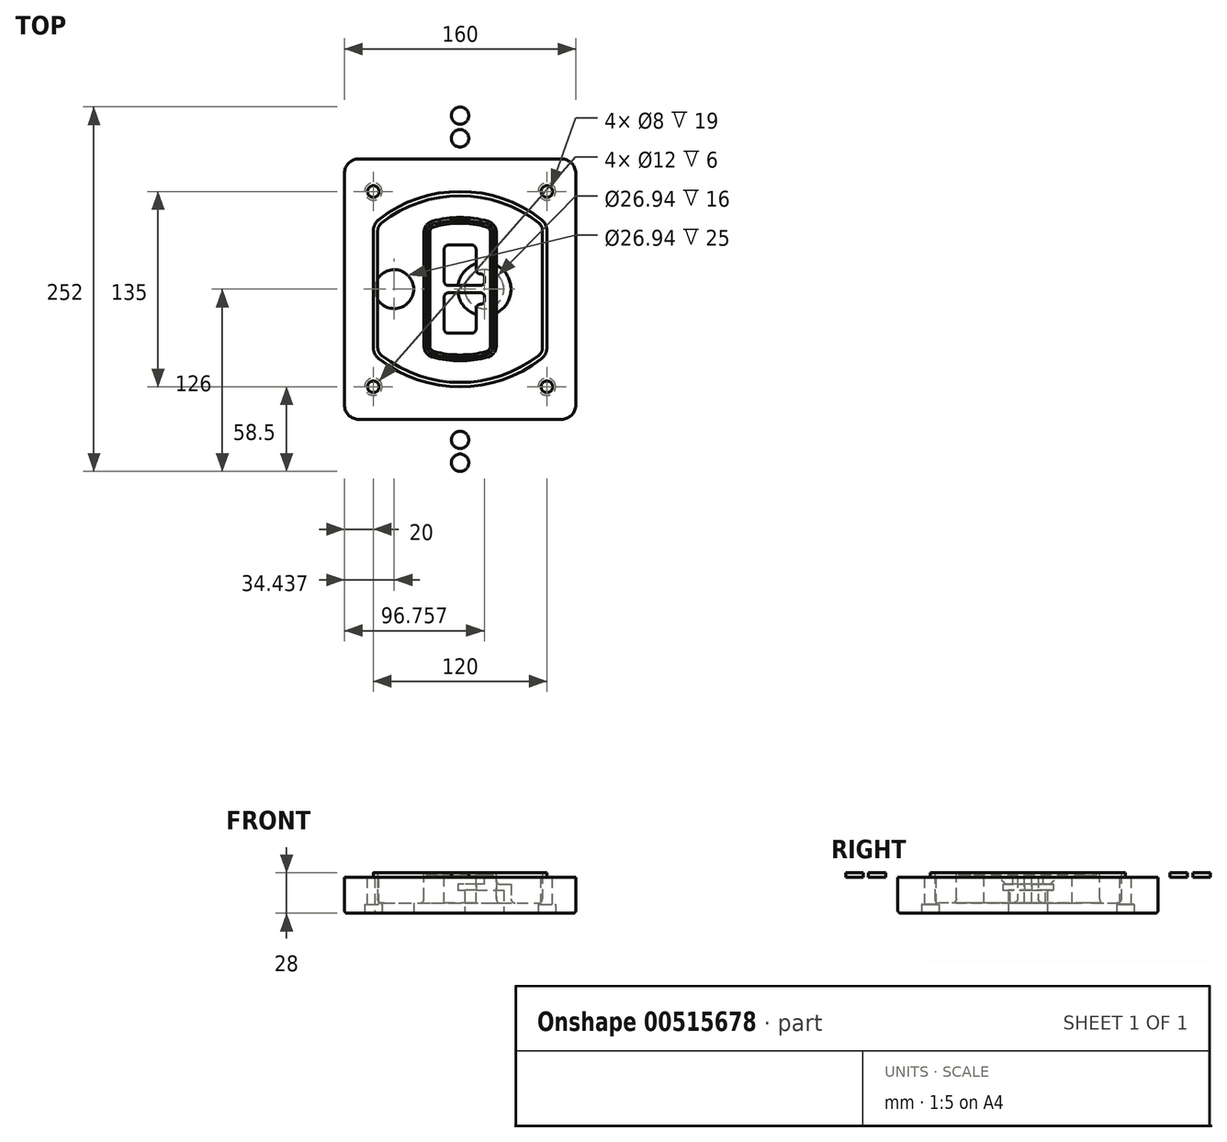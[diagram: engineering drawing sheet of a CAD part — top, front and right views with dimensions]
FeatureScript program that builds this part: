
annotation { "Feature Type Name" : "Feature", "Feature Type Description" : "" }
export const myFeature = defineFeature(function(context is Context, id is Id, definition is map)
    precondition{}
    {
        {
            var Q0;
            Q0=qCreatedBy(makeId("Top.planeOp"),FACE);
            var sketch = newSketch(context, id + "F0", { "sketchPlane" : qUnion([Q0])});
            skPoint(sketch, "E0.rect.middle", {"position": v(0, 0) * mm});
            skLineSegment(sketch, "E1.bottom", {"start": v(-70, -90) * mm, "end": v(70, -90) * mm});
            skLineSegment(sketch, "E1.top", {"start": v(-70, 90) * mm, "end": v(70, 90) * mm});
            skLineSegment(sketch, "E1.left", {"start": v(-80, -80) * mm, "end": v(-80, 80) * mm});
            skLineSegment(sketch, "E1.right", {"start": v(80, -80) * mm, "end": v(80, 80) * mm});
            skLineSegment(sketch, "E2", {"start": v(-80, 90) * mm, "end": v(80, -90) * mm, "construction": true});
            skLineSegment(sketch, "E3", {"start": v(80, 90) * mm, "end": v(-80, -90) * mm, "construction": true});
            skCircle(sketch, "E4", {"center": v(-60, 67.5) * mm, "radius": 4 * mm});
            skCircle(sketch, "E5", {"center": v(60, 67.5) * mm, "radius": 4 * mm});
            skCircle(sketch, "E6", {"center": v(60, -67.5) * mm, "radius": 4 * mm});
            skCircle(sketch, "E7", {"center": v(-60, -67.5) * mm, "radius": 4 * mm});
            skLineSegment(sketch, "E8", {"start": v(-60, 67.5) * mm, "end": v(60, 67.5) * mm, "construction": true});
            skLineSegment(sketch, "E9", {"start": v(60, 67.5) * mm, "end": v(60, -67.5) * mm, "construction": true});
            skLineSegment(sketch, "E10", {"start": v(60, -67.5) * mm, "end": v(-60, -67.5) * mm, "construction": true});
            skLineSegment(sketch, "E11", {"start": v(-60, -67.5) * mm, "end": v(-60, 67.5) * mm, "construction": true});
            skLineSegment(sketch, "E12", {"start": v(-60, 40.3) * mm, "end": v(-60, -40.3) * mm});
            skLineSegment(sketch, "E13", {"start": v(60, 40.3) * mm, "end": v(60, -40.3) * mm});
            skArc(sketch, "E14", {"start": v(56.15, 48.18) * mm, "mid": v(0, 67.5) * mm, "end": v(-56.15, 48.18) * mm});
            skArc(sketch, "E15", {"start": v(-56.15, -48.18) * mm, "mid": v(0, -67.5) * mm, "end": v(56.15, -48.18) * mm});
            skLineSegment(sketch, "E16", {"start": v(-60, 0) * mm, "end": v(60, 0) * mm, "construction": true});
            skPoint(sketch, "E17.visualSharp", {"position": v(-60, -45) * mm});
            skArc(sketch, "E17.filletArc", {"start": v(-60, -40.3) * mm, "mid": v(-58.99, -44.68) * mm, "end": v(-56.15, -48.18) * mm});
            skPoint(sketch, "E18.visualSharp", {"position": v(-60, 45) * mm});
            skArc(sketch, "E18.filletArc", {"start": v(-56.15, 48.18) * mm, "mid": v(-58.99, 44.68) * mm, "end": v(-60, 40.3) * mm});
            skPoint(sketch, "E19.visualSharp", {"position": v(60, 45) * mm});
            skArc(sketch, "E19.filletArc", {"start": v(60, 40.3) * mm, "mid": v(58.99, 44.68) * mm, "end": v(56.15, 48.18) * mm});
            skPoint(sketch, "E20.visualSharp", {"position": v(60, -45) * mm});
            skArc(sketch, "E20.filletArc", {"start": v(56.15, -48.18) * mm, "mid": v(58.99, -44.68) * mm, "end": v(60, -40.3) * mm});
            skPoint(sketch, "E21.visualSharp", {"position": v(-80, 90) * mm});
            skArc(sketch, "E21.filletArc", {"start": v(-70, 90) * mm, "mid": v(-77.07, 87.07) * mm, "end": v(-80, 80) * mm});
            skPoint(sketch, "E22.visualSharp", {"position": v(80, 90) * mm});
            skArc(sketch, "E22.filletArc", {"start": v(80, 80) * mm, "mid": v(77.07, 87.07) * mm, "end": v(70, 90) * mm});
            skPoint(sketch, "E23.visualSharp", {"position": v(80, -90) * mm});
            skArc(sketch, "E23.filletArc", {"start": v(70, -90) * mm, "mid": v(77.07, -87.07) * mm, "end": v(80, -80) * mm});
            skPoint(sketch, "E24.visualSharp", {"position": v(-80, -90) * mm});
            skArc(sketch, "E24.filletArc", {"start": v(-80, -80) * mm, "mid": v(-77.07, -87.07) * mm, "end": v(-70, -90) * mm});
            skArc(sketch, "E25.0", {"start": v(57, 40.3) * mm, "mid": v(56.3, 43.36) * mm, "end": v(54.3, 45.81) * mm});
            skLineSegment(sketch, "E25.1", {"start": v(57, 40.3) * mm, "end": v(57, -40.3) * mm});
            skArc(sketch, "E25.2", {"start": v(54.3, -45.81) * mm, "mid": v(56.3, -43.36) * mm, "end": v(57, -40.3) * mm});
            skArc(sketch, "E25.3", {"start": v(-54.3, -45.81) * mm, "mid": v(0, -64.5) * mm, "end": v(54.3, -45.81) * mm});
            skArc(sketch, "E25.4", {"start": v(-57, -40.3) * mm, "mid": v(-56.3, -43.36) * mm, "end": v(-54.3, -45.81) * mm});
            skArc(sketch, "E25.5", {"start": v(54.3, 45.81) * mm, "mid": v(0, 64.5) * mm, "end": v(-54.3, 45.81) * mm});
            skLineSegment(sketch, "E25.6", {"start": v(-57, 40.3) * mm, "end": v(-57, -40.3) * mm});
            skArc(sketch, "E25.7", {"start": v(-54.3, 45.81) * mm, "mid": v(-56.3, 43.36) * mm, "end": v(-57, 40.3) * mm});
            skArc(sketch, "E26.0", {"start": v(-58.62, 51.33) * mm, "mid": v(-62.58, 46.43) * mm, "end": v(-64, 40.3) * mm});
            skArc(sketch, "E26.1", {"start": v(58.62, 51.33) * mm, "mid": v(0, 71.5) * mm, "end": v(-58.62, 51.33) * mm});
            skArc(sketch, "E26.2", {"start": v(64, 40.3) * mm, "mid": v(62.58, 46.43) * mm, "end": v(58.62, 51.33) * mm});
            skLineSegment(sketch, "E26.3", {"start": v(64, 40.3) * mm, "end": v(64, -40.3) * mm});
            skArc(sketch, "E26.4", {"start": v(58.62, -51.33) * mm, "mid": v(62.58, -46.43) * mm, "end": v(64, -40.3) * mm});
            skLineSegment(sketch, "E26.5", {"start": v(-64, 40.3) * mm, "end": v(-64, -40.3) * mm});
            skArc(sketch, "E26.6", {"start": v(-58.62, -51.33) * mm, "mid": v(0, -71.5) * mm, "end": v(58.62, -51.33) * mm});
            skArc(sketch, "E26.7", {"start": v(-64, -40.3) * mm, "mid": v(-62.58, -46.43) * mm, "end": v(-58.62, -51.33) * mm});
            skSolve(sketch);
        }
        {
            var Q0;
            Q0=makeQuery(id+"F0.imprint","IMPRINT",FACE,{"disambiguationData":[TD([[makeQuery(id+"F0.imprint","IMPRINT",EDGE,{"derivedFrom":sQuery(id+"F0.wireOp",EDGE,"E1.bottom")}),1.0]])]});
            var Q1;
            Q1=makeQuery(id+"F0.imprint","IMPRINT",FACE,{"disambiguationData":[TD([[makeQuery(id+"F0.imprint","IMPRINT",EDGE,{"derivedFrom":sQuery(id+"F0.wireOp",EDGE,"E12")}),1.0]])]});
            var Q2;
            Q2=makeQuery(id+"F0.imprint","IMPRINT",FACE,{"disambiguationData":[TD([[makeQuery(id+"F0.imprint","IMPRINT",EDGE,{"derivedFrom":sQuery(id+"F0.wireOp",EDGE,"E25.0")}),1.0]])]});
            var Q3;
            Q3=makeQuery(id+"F0.imprint","IMPRINT",FACE,{"disambiguationData":[TD([[makeQuery(id+"F0.imprint","IMPRINT",EDGE,{"derivedFrom":sQuery(id+"F0.wireOp",EDGE,"E12")}),-1.0]])]});
            extrude(context, id + "F1", {"entities" : qUnion([Q0, Q1, Q2, Q3]), "oppositeDirection" : true, "depth" : 25 * mm});
        }
        {
            var Q0;
            Q0=makeQuery(id+"F0.imprint","IMPRINT",FACE,{"disambiguationData":[TD([[makeQuery(id+"F0.imprint","IMPRINT",EDGE,{"derivedFrom":sQuery(id+"F0.wireOp",EDGE,"E12")}),1.0]])]});
            extrude(context, id + "F2", {"entities" : qUnion([Q0]), "operationType" : NewBodyOperationType.ADD, "depth" : 3 * mm});
        }
        {
            var Q0;
            Q0=makeQuery(id+"F0.imprint","IMPRINT",FACE,{"disambiguationData":[TD([[makeQuery(id+"F0.imprint","IMPRINT",EDGE,{"derivedFrom":sQuery(id+"F0.wireOp",EDGE,"E25.0")}),1.0]])]});
            extrude(context, id + "F3", {"entities" : qUnion([Q0]), "operationType" : NewBodyOperationType.REMOVE, "oppositeDirection" : true, "depth" : 18 * mm});
        }
        {
            var Q0;
            Q0=makeQuery(id+"F2.opExtrude","CAP_FACE",FACE,{"disambiguationData":[OSD([sQuery(id+"F0.wireOp",EDGE,"E12"),sQuery(id+"F0.wireOp",EDGE,"E13"),sQuery(id+"F0.wireOp",EDGE,"E14"),sQuery(id+"F0.wireOp",EDGE,"E15"),sQuery(id+"F0.wireOp",EDGE,"E17.filletArc"),sQuery(id+"F0.wireOp",EDGE,"E18.filletArc"),sQuery(id+"F0.wireOp",EDGE,"E19.filletArc"),sQuery(id+"F0.wireOp",EDGE,"E20.filletArc"),sQuery(id+"F0.wireOp",EDGE,"E25.0"),sQuery(id+"F0.wireOp",EDGE,"E25.1"),sQuery(id+"F0.wireOp",EDGE,"E25.2"),sQuery(id+"F0.wireOp",EDGE,"E25.3"),sQuery(id+"F0.wireOp",EDGE,"E25.4"),sQuery(id+"F0.wireOp",EDGE,"E25.5"),sQuery(id+"F0.wireOp",EDGE,"E25.6"),sQuery(id+"F0.wireOp",EDGE,"E25.7")])],"isStart":false});
            var sketch = newSketch(context, id + "F4", { "sketchPlane" : qUnion([Q0])});
            skArc(sketch, "E27.0", {"start": v(-19.08, -46.97) * mm, "mid": v(0, -49.5) * mm, "end": v(19.08, -46.97) * mm});
            skArc(sketch, "E28.0", {"start": v(19.08, 46.97) * mm, "mid": v(0, 49.5) * mm, "end": v(-19.08, 46.97) * mm});
            skLineSegment(sketch, "E29", {"start": v(-25, 39.25) * mm, "end": v(-25, -39.25) * mm});
            skLineSegment(sketch, "E30", {"start": v(25, 39.25) * mm, "end": v(25, -39.25) * mm});
            skLineSegment(sketch, "E31", {"start": v(-25, 45.1) * mm, "end": v(25, 45.1) * mm, "construction": true});
            skLineSegment(sketch, "E32", {"start": v(-25, -45.1) * mm, "end": v(25, -45.1) * mm, "construction": true});
            skPoint(sketch, "E33.visualSharp", {"position": v(-25, 45.1) * mm});
            skArc(sketch, "E33.filletArc", {"start": v(-19.08, 46.97) * mm, "mid": v(-23.35, 44.11) * mm, "end": v(-25, 39.25) * mm});
            skPoint(sketch, "E34.visualSharp", {"position": v(25, 45.1) * mm});
            skArc(sketch, "E34.filletArc", {"start": v(25, 39.25) * mm, "mid": v(23.35, 44.11) * mm, "end": v(19.08, 46.97) * mm});
            skPoint(sketch, "E35.visualSharp", {"position": v(25, -45.1) * mm});
            skArc(sketch, "E35.filletArc", {"start": v(19.08, -46.97) * mm, "mid": v(23.35, -44.11) * mm, "end": v(25, -39.25) * mm});
            skPoint(sketch, "E36.visualSharp", {"position": v(-25, -45.1) * mm});
            skArc(sketch, "E36.filletArc", {"start": v(-25, -39.25) * mm, "mid": v(-23.35, -44.11) * mm, "end": v(-19.08, -46.97) * mm});
            skArc(sketch, "E37.0", {"start": v(54.3, 45.81) * mm, "mid": v(0, 64.5) * mm, "end": v(-54.3, 45.81) * mm});
            skArc(sketch, "E37.1", {"start": v(-54.3, 45.81) * mm, "mid": v(-56.3, 43.36) * mm, "end": v(-57, 40.3) * mm});
            skLineSegment(sketch, "E37.2", {"start": v(-57, 40.3) * mm, "end": v(-57, -40.3) * mm});
            skArc(sketch, "E37.3", {"start": v(-57, -40.3) * mm, "mid": v(-56.3, -43.36) * mm, "end": v(-54.3, -45.81) * mm});
            skArc(sketch, "E37.4", {"start": v(-54.3, -45.81) * mm, "mid": v(0, -64.5) * mm, "end": v(54.3, -45.81) * mm});
            skArc(sketch, "E37.5", {"start": v(54.3, -45.81) * mm, "mid": v(56.3, -43.36) * mm, "end": v(57, -40.3) * mm});
            skLineSegment(sketch, "E37.6", {"start": v(57, 40.3) * mm, "end": v(57, -40.3) * mm});
            skArc(sketch, "E37.7", {"start": v(57, 40.3) * mm, "mid": v(56.3, 43.36) * mm, "end": v(54.3, 45.81) * mm});
            skLineSegment(sketch, "E38.0", {"start": v(23, 39.25) * mm, "end": v(23, -39.25) * mm});
            skArc(sketch, "E38.1", {"start": v(18.56, -45.04) * mm, "mid": v(21.76, -42.9) * mm, "end": v(23, -39.25) * mm});
            skArc(sketch, "E38.2", {"start": v(-18.56, -45.04) * mm, "mid": v(0, -47.5) * mm, "end": v(18.56, -45.04) * mm});
            skArc(sketch, "E38.3", {"start": v(-23, -39.25) * mm, "mid": v(-21.76, -42.9) * mm, "end": v(-18.56, -45.04) * mm});
            skLineSegment(sketch, "E38.4", {"start": v(-23, 39.25) * mm, "end": v(-23, -39.25) * mm});
            skArc(sketch, "E38.5", {"start": v(23, 39.25) * mm, "mid": v(21.76, 42.9) * mm, "end": v(18.56, 45.04) * mm});
            skArc(sketch, "E38.6", {"start": v(-18.56, 45.04) * mm, "mid": v(-21.76, 42.9) * mm, "end": v(-23, 39.25) * mm});
            skArc(sketch, "E38.7", {"start": v(18.56, 45.04) * mm, "mid": v(0, 47.5) * mm, "end": v(-18.56, 45.04) * mm});
            skArc(sketch, "E39.0", {"start": v(21, 39.25) * mm, "mid": v(20.18, 41.68) * mm, "end": v(18.04, 43.1) * mm});
            skLineSegment(sketch, "E39.1", {"start": v(21, 39.25) * mm, "end": v(21, -39.25) * mm});
            skArc(sketch, "E39.2", {"start": v(18.04, -43.1) * mm, "mid": v(20.18, -41.68) * mm, "end": v(21, -39.25) * mm});
            skArc(sketch, "E39.3", {"start": v(-18.04, -43.1) * mm, "mid": v(0, -45.5) * mm, "end": v(18.04, -43.1) * mm});
            skArc(sketch, "E39.4", {"start": v(-21, -39.25) * mm, "mid": v(-20.18, -41.68) * mm, "end": v(-18.04, -43.1) * mm});
            skArc(sketch, "E39.5", {"start": v(18.04, 43.1) * mm, "mid": v(0, 45.5) * mm, "end": v(-18.04, 43.1) * mm});
            skLineSegment(sketch, "E39.6", {"start": v(-21, 39.25) * mm, "end": v(-21, -39.25) * mm});
            skArc(sketch, "E39.7", {"start": v(-18.04, 43.1) * mm, "mid": v(-20.18, 41.68) * mm, "end": v(-21, 39.25) * mm});
            skLineSegment(sketch, "E40", {"start": v(-25, 0) * mm, "end": v(25, 0) * mm, "construction": true});
            skLineSegment(sketch, "E41", {"start": v(-11, 5.5) * mm, "end": v(-11, 27.5) * mm});
            skLineSegment(sketch, "E42", {"start": v(-8, 30.5) * mm, "end": v(8, 30.5) * mm});
            skLineSegment(sketch, "E43", {"start": v(11, 27.5) * mm, "end": v(11, 13.5) * mm});
            skLineSegment(sketch, "E44", {"start": v(14, 10.5) * mm, "end": v(14, 10.5) * mm});
            skLineSegment(sketch, "E45", {"start": v(17, 7.5) * mm, "end": v(17, 5.5) * mm});
            skLineSegment(sketch, "E46", {"start": v(14, 2.5) * mm, "end": v(-8, 2.5) * mm});
            skPoint(sketch, "E47.visualSharp", {"position": v(-11, 30.5) * mm});
            skArc(sketch, "E47.filletArc", {"start": v(-8, 30.5) * mm, "mid": v(-10.12, 29.62) * mm, "end": v(-11, 27.5) * mm});
            skPoint(sketch, "E48.visualSharp", {"position": v(11, 30.5) * mm});
            skArc(sketch, "E48.filletArc", {"start": v(11, 27.5) * mm, "mid": v(10.12, 29.62) * mm, "end": v(8, 30.5) * mm});
            skPoint(sketch, "E49.visualSharp", {"position": v(11, 10.5) * mm});
            skArc(sketch, "E49.filletArc", {"start": v(11, 13.5) * mm, "mid": v(11.88, 11.38) * mm, "end": v(14, 10.5) * mm});
            skPoint(sketch, "E50.visualSharp", {"position": v(17, 10.5) * mm});
            skArc(sketch, "E50.filletArc", {"start": v(17, 7.5) * mm, "mid": v(16.12, 9.62) * mm, "end": v(14, 10.5) * mm});
            skPoint(sketch, "E51.visualSharp", {"position": v(17, 2.5) * mm});
            skArc(sketch, "E51.filletArc", {"start": v(14, 2.5) * mm, "mid": v(16.12, 3.38) * mm, "end": v(17, 5.5) * mm});
            skPoint(sketch, "E52.visualSharp", {"position": v(-11, 2.5) * mm});
            skArc(sketch, "E52.filletArc", {"start": v(-11, 5.5) * mm, "mid": v(-10.12, 3.38) * mm, "end": v(-8, 2.5) * mm});
            skLineSegment(sketch, "E53.0.MirrorCS", {"start": v(14, -2.5) * mm, "end": v(-8, -2.5) * mm});
            skArc(sketch, "E54.0.MirrorCS", {"start": v(-11, -5.5) * mm, "mid": v(-10.12, -3.38) * mm, "end": v(-8, -2.5) * mm});
            skLineSegment(sketch, "E55.0.MirrorCS", {"start": v(-11, -5.5) * mm, "end": v(-11, -27.5) * mm});
            skArc(sketch, "E56.0.MirrorCS", {"start": v(-8, -30.5) * mm, "mid": v(-10.12, -29.62) * mm, "end": v(-11, -27.5) * mm});
            skLineSegment(sketch, "E57.0.MirrorCS", {"start": v(-8, -30.5) * mm, "end": v(8, -30.5) * mm});
            skArc(sketch, "E58.0.MirrorCS", {"start": v(11, -27.5) * mm, "mid": v(10.12, -29.62) * mm, "end": v(8, -30.5) * mm});
            skLineSegment(sketch, "E59.0.MirrorCS", {"start": v(11, -27.5) * mm, "end": v(11, -13.5) * mm});
            skArc(sketch, "E60.0.MirrorCS", {"start": v(11, -13.5) * mm, "mid": v(11.88, -11.38) * mm, "end": v(14, -10.5) * mm});
            skArc(sketch, "E61.0.MirrorCS", {"start": v(17, -7.5) * mm, "mid": v(16.12, -9.62) * mm, "end": v(14, -10.5) * mm});
            skLineSegment(sketch, "E62.0.MirrorCS", {"start": v(17, -7.5) * mm, "end": v(17, -5.5) * mm});
            skArc(sketch, "E63.0.MirrorCS", {"start": v(14, -2.5) * mm, "mid": v(16.12, -3.38) * mm, "end": v(17, -5.5) * mm});
            skSolve(sketch);
        }
        {
            var Q0;
            Q0=makeQuery(id+"F4.imprint","IMPRINT",FACE,{"disambiguationData":[TD([[makeQuery(id+"F4.imprint","IMPRINT",EDGE,{"derivedFrom":sQuery(id+"F4.wireOp",EDGE,"E27.0")}),1.0]])]});
            var Q1;
            Q1=makeQuery(id+"F4.imprint","IMPRINT",FACE,{"disambiguationData":[TD([[makeQuery(id+"F4.imprint","IMPRINT",EDGE,{"derivedFrom":sQuery(id+"F4.wireOp",EDGE,"E38.0")}),-1.0]])]});
            var Q2;
            Q2=makeQuery(id+"F4.imprint","IMPRINT",FACE,{"disambiguationData":[TD([[makeQuery(id+"F4.imprint","IMPRINT",EDGE,{"derivedFrom":sQuery(id+"F4.wireOp",EDGE,"E39.0")}),1.0]])]});
            extrude(context, id + "F5", {"entities" : qUnion([Q0, Q1, Q2]), "operationType" : NewBodyOperationType.ADD, "endBound" : BoundingType.UP_TO_NEXT, "oppositeDirection" : true, "depth" : 25 * mm});
        }
        {
            var Q0;
            Q0=makeQuery(id+"F4.imprint","IMPRINT",FACE,{"disambiguationData":[TD([[makeQuery(id+"F4.imprint","IMPRINT",EDGE,{"derivedFrom":sQuery(id+"F4.wireOp",EDGE,"E38.0")}),-1.0]])]});
            extrude(context, id + "F6", {"entities" : qUnion([Q0]), "operationType" : NewBodyOperationType.REMOVE, "oppositeDirection" : true, "depth" : 2 * mm});
        }
        {
            var Q0;
            Q0=makeQuery(id+"F1.opExtrude","CAP_FACE",FACE,{"disambiguationData":[OSD([sQuery(id+"F0.wireOp",EDGE,"E1.bottom"),sQuery(id+"F0.wireOp",EDGE,"E1.top"),sQuery(id+"F0.wireOp",EDGE,"E1.left"),sQuery(id+"F0.wireOp",EDGE,"E1.right"),sQuery(id+"F0.wireOp",EDGE,"E4"),sQuery(id+"F0.wireOp",EDGE,"E5"),sQuery(id+"F0.wireOp",EDGE,"E6"),sQuery(id+"F0.wireOp",EDGE,"E7"),sQuery(id+"F0.wireOp",EDGE,"E21.filletArc"),sQuery(id+"F0.wireOp",EDGE,"E22.filletArc"),sQuery(id+"F0.wireOp",EDGE,"E23.filletArc"),sQuery(id+"F0.wireOp",EDGE,"E24.filletArc")])],"isStart":false});
            var sketch = newSketch(context, id + "F7", { "sketchPlane" : qUnion([Q0])});
            skCircle(sketch, "E64", {"center": v(16.76, 0) * mm, "radius": 13.47 * mm});
            skCircle(sketch, "E65", {"center": v(-45.56, 0) * mm, "radius": 13.47 * mm});
            skLineSegment(sketch, "E66", {"start": v(80, 0) * mm, "end": v(-80, 0) * mm});
            skCircle(sketch, "E67", {"center": v(16.76, 0) * mm, "radius": 18.47 * mm});
            skCircle(sketch, "E68", {"center": v(60, -67.5) * mm, "radius": 6 * mm});
            skCircle(sketch, "E69", {"center": v(-60, -67.5) * mm, "radius": 6 * mm});
            skCircle(sketch, "E70", {"center": v(-60, 67.5) * mm, "radius": 6 * mm});
            skCircle(sketch, "E71", {"center": v(60, 67.5) * mm, "radius": 6 * mm});
            skSolve(sketch);
        }
        {
            var Q0;
            {var subQ1=sQuery(id+"F7.wireOp",EDGE,"E66");var subQ4=sQuery(id+"F7.wireOp",EDGE,"E64");var subQ6=makeQuery(id+"F7.imprint","INTERSECT",VERTEX,{"disambiguationData":[OD(0.0)],"derivedFrom":[subQ4,subQ1]});Q0=makeQuery(id+"F7.imprint","IMPRINT",FACE,{"disambiguationData":[TD([[makeQuery(id+"F7.imprint","IMPRINT",EDGE,{"disambiguationData":[TD([[subQ6,-1.0]])],"derivedFrom":subQ4}),-1.0]])]});}
            var Q1;
            {var subQ0=sQuery(id+"F7.wireOp",EDGE,"E66");var subQ1=sQuery(id+"F7.wireOp",EDGE,"E64");var subQ3=makeQuery(id+"F7.imprint","INTERSECT",VERTEX,{"disambiguationData":[OD(0.0)],"derivedFrom":[subQ1,subQ0]});Q1=makeQuery(id+"F7.imprint","IMPRINT",FACE,{"disambiguationData":[TD([[makeQuery(id+"F7.imprint","IMPRINT",EDGE,{"disambiguationData":[TD([[subQ3,-1.0]])],"derivedFrom":subQ1}),1.0]])]});}
            var Q2;
            {var subQ0=sQuery(id+"F7.wireOp",EDGE,"E66");var subQ1=sQuery(id+"F7.wireOp",EDGE,"E64");var subQ3=makeQuery(id+"F7.imprint","INTERSECT",VERTEX,{"disambiguationData":[OD(0.0)],"derivedFrom":[subQ1,subQ0]});Q2=makeQuery(id+"F7.imprint","IMPRINT",FACE,{"disambiguationData":[TD([[makeQuery(id+"F7.imprint","IMPRINT",EDGE,{"disambiguationData":[TD([[subQ3,1.0]])],"derivedFrom":subQ1}),1.0]])]});}
            var Q3;
            {var subQ1=sQuery(id+"F7.wireOp",EDGE,"E66");var subQ4=sQuery(id+"F7.wireOp",EDGE,"E64");var subQ6=makeQuery(id+"F7.imprint","INTERSECT",VERTEX,{"disambiguationData":[OD(0.0)],"derivedFrom":[subQ4,subQ1]});Q3=makeQuery(id+"F7.imprint","IMPRINT",FACE,{"disambiguationData":[TD([[makeQuery(id+"F7.imprint","IMPRINT",EDGE,{"disambiguationData":[TD([[subQ6,1.0]])],"derivedFrom":subQ4}),-1.0]])]});}
            extrude(context, id + "F8", {"entities" : qUnion([Q0, Q1, Q2, Q3]), "operationType" : NewBodyOperationType.ADD, "oppositeDirection" : true, "depth" : 20 * mm});
        }
        {
            var Q0;
            {var subQ0=sQuery(id+"F7.wireOp",EDGE,"E66");var subQ1=sQuery(id+"F7.wireOp",EDGE,"E64");var subQ3=makeQuery(id+"F7.imprint","INTERSECT",VERTEX,{"disambiguationData":[OD(0.0)],"derivedFrom":[subQ1,subQ0]});Q0=makeQuery(id+"F7.imprint","IMPRINT",FACE,{"disambiguationData":[TD([[makeQuery(id+"F7.imprint","IMPRINT",EDGE,{"disambiguationData":[TD([[subQ3,-1.0]])],"derivedFrom":subQ1}),1.0]])]});}
            var Q1;
            {var subQ0=sQuery(id+"F7.wireOp",EDGE,"E66");var subQ1=sQuery(id+"F7.wireOp",EDGE,"E64");var subQ3=makeQuery(id+"F7.imprint","INTERSECT",VERTEX,{"disambiguationData":[OD(0.0)],"derivedFrom":[subQ1,subQ0]});Q1=makeQuery(id+"F7.imprint","IMPRINT",FACE,{"disambiguationData":[TD([[makeQuery(id+"F7.imprint","IMPRINT",EDGE,{"disambiguationData":[TD([[subQ3,1.0]])],"derivedFrom":subQ1}),1.0]])]});}
            extrude(context, id + "F9", {"entities" : qUnion([Q0, Q1]), "operationType" : NewBodyOperationType.REMOVE, "oppositeDirection" : true, "depth" : 16 * mm});
        }
        {
            var Q0;
            {var subQ0=sQuery(id+"F7.wireOp",EDGE,"E66");var subQ1=sQuery(id+"F7.wireOp",EDGE,"E65");var subQ3=makeQuery(id+"F7.imprint","INTERSECT",VERTEX,{"disambiguationData":[OD(0.0)],"derivedFrom":[subQ1,subQ0]});Q0=makeQuery(id+"F7.imprint","IMPRINT",FACE,{"disambiguationData":[TD([[makeQuery(id+"F7.imprint","IMPRINT",EDGE,{"disambiguationData":[TD([[subQ3,-1.0]])],"derivedFrom":subQ1}),1.0]])]});}
            var Q1;
            {var subQ0=sQuery(id+"F7.wireOp",EDGE,"E66");var subQ1=sQuery(id+"F7.wireOp",EDGE,"E65");var subQ3=makeQuery(id+"F7.imprint","INTERSECT",VERTEX,{"disambiguationData":[OD(0.0)],"derivedFrom":[subQ1,subQ0]});Q1=makeQuery(id+"F7.imprint","IMPRINT",FACE,{"disambiguationData":[TD([[makeQuery(id+"F7.imprint","IMPRINT",EDGE,{"disambiguationData":[TD([[subQ3,1.0]])],"derivedFrom":subQ1}),1.0]])]});}
            extrude(context, id + "F10", {"entities" : qUnion([Q0, Q1]), "operationType" : NewBodyOperationType.REMOVE, "oppositeDirection" : true, "depth" : 25 * mm});
        }
        {
            var Q0;
            Q0=makeQuery(id+"F7.imprint","IMPRINT",FACE,{"disambiguationData":[TD([[makeQuery(id+"F7.imprint","IMPRINT",EDGE,{"derivedFrom":sQuery(id+"F7.wireOp",EDGE,"E68")}),1.0]])]});
            var Q1;
            Q1=makeQuery(id+"F7.imprint","IMPRINT",FACE,{"disambiguationData":[TD([[makeQuery(id+"F7.imprint","IMPRINT",EDGE,{"derivedFrom":makeQuery(id+"F1.opExtrude","CAP_EDGE",EDGE,{"disambiguationData":[OSD([sQuery(id+"F0.wireOp",EDGE,"E5")])],"isStart":false})}),-1.0]])]});
            var Q2;
            Q2=makeQuery(id+"F7.imprint","IMPRINT",FACE,{"disambiguationData":[TD([[makeQuery(id+"F7.imprint","IMPRINT",EDGE,{"derivedFrom":sQuery(id+"F7.wireOp",EDGE,"E69")}),1.0]])]});
            var Q3;
            Q3=makeQuery(id+"F7.imprint","IMPRINT",FACE,{"disambiguationData":[TD([[makeQuery(id+"F7.imprint","IMPRINT",EDGE,{"derivedFrom":makeQuery(id+"F1.opExtrude","CAP_EDGE",EDGE,{"disambiguationData":[OSD([sQuery(id+"F0.wireOp",EDGE,"E4")])],"isStart":false})}),-1.0]])]});
            var Q4;
            Q4=makeQuery(id+"F7.imprint","IMPRINT",FACE,{"disambiguationData":[TD([[makeQuery(id+"F7.imprint","IMPRINT",EDGE,{"derivedFrom":sQuery(id+"F7.wireOp",EDGE,"E70")}),1.0]])]});
            var Q5;
            Q5=makeQuery(id+"F7.imprint","IMPRINT",FACE,{"disambiguationData":[TD([[makeQuery(id+"F7.imprint","IMPRINT",EDGE,{"derivedFrom":makeQuery(id+"F1.opExtrude","CAP_EDGE",EDGE,{"disambiguationData":[OSD([sQuery(id+"F0.wireOp",EDGE,"E7")])],"isStart":false})}),-1.0]])]});
            var Q6;
            Q6=makeQuery(id+"F7.imprint","IMPRINT",FACE,{"disambiguationData":[TD([[makeQuery(id+"F7.imprint","IMPRINT",EDGE,{"derivedFrom":sQuery(id+"F7.wireOp",EDGE,"E71")}),1.0]])]});
            var Q7;
            Q7=makeQuery(id+"F7.imprint","IMPRINT",FACE,{"disambiguationData":[TD([[makeQuery(id+"F7.imprint","IMPRINT",EDGE,{"derivedFrom":makeQuery(id+"F1.opExtrude","CAP_EDGE",EDGE,{"disambiguationData":[OSD([sQuery(id+"F0.wireOp",EDGE,"E6")])],"isStart":false})}),-1.0]])]});
            extrude(context, id + "F11", {"entities" : qUnion([Q0, Q1, Q2, Q3, Q4, Q5, Q6, Q7]), "operationType" : NewBodyOperationType.REMOVE, "oppositeDirection" : true, "depth" : 6 * mm});
        }
        {
            var Q0;
            Q0=makeQuery(id+"F9.boolean.opBoolean","COPY",FACE,{"derivedFrom":makeQuery(id+"F9.opExtrude","CAP_FACE",FACE,{"disambiguationData":[OSD([sQuery(id+"F7.wireOp",EDGE,"E64")])],"isStart":false})});
            var sketch = newSketch(context, id + "F12", { "sketchPlane" : qUnion([Q0])});
            skArc(sketch, "E72.0", {"start": v(11, 17.55) * mm, "mid": v(2.57, 11.82) * mm, "end": v(-1.54, 2.5) * mm});
            skArc(sketch, "E72.1", {"start": v(-1.54, -2.5) * mm, "mid": v(2.57, -11.82) * mm, "end": v(11, -17.55) * mm});
            skLineSegment(sketch, "E73", {"start": v(-1.54, -2.5) * mm, "end": v(14, -2.5) * mm});
            skLineSegment(sketch, "E74.0", {"start": v(14, 2.5) * mm, "end": v(-1.54, 2.5) * mm});
            skArc(sketch, "E74.1", {"start": v(14, 2.5) * mm, "mid": v(16.12, 3.38) * mm, "end": v(17, 5.5) * mm});
            skLineSegment(sketch, "E74.2", {"start": v(17, 7.5) * mm, "end": v(17, 5.5) * mm});
            skArc(sketch, "E74.3", {"start": v(17, 7.5) * mm, "mid": v(16.12, 9.62) * mm, "end": v(14, 10.5) * mm});
            skArc(sketch, "E74.4", {"start": v(11, 13.5) * mm, "mid": v(11.88, 11.38) * mm, "end": v(14, 10.5) * mm});
            skLineSegment(sketch, "E74.5", {"start": v(11, 17.55) * mm, "end": v(11, 13.5) * mm});
            skLineSegment(sketch, "E74.7", {"start": v(14, -2.5) * mm, "end": v(-1.54, -2.5) * mm});
            skArc(sketch, "E74.8", {"start": v(14, -2.5) * mm, "mid": v(16.12, -3.38) * mm, "end": v(17, -5.5) * mm});
            skLineSegment(sketch, "E74.9", {"start": v(17, -7.5) * mm, "end": v(17, -5.5) * mm});
            skArc(sketch, "E74.10", {"start": v(17, -7.5) * mm, "mid": v(16.12, -9.62) * mm, "end": v(14, -10.5) * mm});
            skArc(sketch, "E74.11", {"start": v(11, -13.5) * mm, "mid": v(11.88, -11.38) * mm, "end": v(14, -10.5) * mm});
            skLineSegment(sketch, "E74.12", {"start": v(11, -17.55) * mm, "end": v(11, -13.5) * mm});
            skPoint(sketch, "E75.orphan", {"position": v(11, -27.5) * mm});
            skPoint(sketch, "E76.orphan", {"position": v(-8, -2.5) * mm});
            skPoint(sketch, "E77.orphan", {"position": v(-8, 2.5) * mm});
            skPoint(sketch, "E78.orphan", {"position": v(11, 27.5) * mm});
            skSolve(sketch);
        }
        {
            var Q0;
            {var subQ7=sQuery(id+"F12.wireOp",EDGE,"E72.0");var subQ14=sQuery(id+"F12.wireOp",EDGE,"E72.1");var subQ16=sQuery(id+"F12.wireOp",EDGE,"E74.1");var subQ18=sQuery(id+"F12.wireOp",EDGE,"E74.8");Q0=qUnion([makeQuery(id+"F12.imprint","IMPRINT",FACE,{"disambiguationData":[TD([[makeQuery(id+"F12.imprint","IMPRINT",EDGE,{"derivedFrom":subQ7}),1.0]])]}),makeQuery(id+"F12.imprint","IMPRINT",FACE,{"disambiguationData":[TD([[makeQuery(id+"F12.imprint","IMPRINT",EDGE,{"derivedFrom":subQ14}),1.0]])]}),makeQuery(id+"F12.imprint","IMPRINT",FACE,{"disambiguationData":[TD([[makeQuery(id+"F12.imprint","IMPRINT",EDGE,{"derivedFrom":subQ16}),1.0]])]}),makeQuery(id+"F12.imprint","IMPRINT",FACE,{"disambiguationData":[TD([[makeQuery(id+"F12.imprint","IMPRINT",EDGE,{"derivedFrom":subQ18}),-1.0]])]})]);}
            var Q1;
            Q1=makeQuery(id+"F5.boolean.opBoolean","SPLIT",FACE,{"disambiguationData":[TD([makeQuery(id+"F5.opExtrude","SWEPT_FACE",FACE,{"disambiguationData":[OSD([sQuery(id+"F4.wireOp",EDGE,"E41")])]})])],"derivedFrom":makeQuery(id+"F3.boolean.opBoolean","COPY",FACE,{"derivedFrom":makeQuery(id+"F3.opExtrude","CAP_FACE",FACE,{"disambiguationData":[OSD([sQuery(id+"F0.wireOp",EDGE,"E25.0"),sQuery(id+"F0.wireOp",EDGE,"E25.1"),sQuery(id+"F0.wireOp",EDGE,"E25.2"),sQuery(id+"F0.wireOp",EDGE,"E25.3"),sQuery(id+"F0.wireOp",EDGE,"E25.4"),sQuery(id+"F0.wireOp",EDGE,"E25.5"),sQuery(id+"F0.wireOp",EDGE,"E25.6"),sQuery(id+"F0.wireOp",EDGE,"E25.7")])],"isStart":false})})});
            extrude(context, id + "F13", {"entities" : qUnion([Q0]), "operationType" : NewBodyOperationType.REMOVE, "endBound" : BoundingType.UP_TO_SURFACE, "endBoundEntityFace" : qUnion([Q1]), "depth" : 25 * mm});
        }
        {
            var Q0;
            Q0=makeQuery(id+"F3.boolean.opBoolean","COPY",EDGE,{"derivedFrom":makeQuery(id+"F3.opExtrude","CAP_EDGE",EDGE,{"disambiguationData":[OSD([sQuery(id+"F0.wireOp",EDGE,"E25.6")])],"isStart":false})});
            var Q1;
            Q1=makeQuery(id+"F8.boolean.opBoolean","INTERSECT",EDGE,{"derivedFrom":[makeQuery(id+"F5.opExtrude","SWEPT_FACE",FACE,{"disambiguationData":[OSD([sQuery(id+"F4.wireOp",EDGE,"E30")])]}),makeQuery(id+"F8.opExtrude","CAP_FACE",FACE,{"disambiguationData":[OSD([sQuery(id+"F7.wireOp",EDGE,"E67")])],"isStart":false})]});
            var Q2;
            Q2=makeQuery(id+"F8.boolean.opBoolean","INTERSECT",EDGE,{"disambiguationData":[OD(1.0)],"derivedFrom":[makeQuery(id+"F5.opExtrude","SWEPT_FACE",FACE,{"disambiguationData":[OSD([sQuery(id+"F4.wireOp",EDGE,"E30")])]}),makeQuery(id+"F8.opExtrude","SWEPT_FACE",FACE,{"disambiguationData":[OSD([sQuery(id+"F7.wireOp",EDGE,"E67")])]})]});
            var Q3;
            {var subQ0=sQuery(id+"F4.wireOp",EDGE,"E30");Q3=makeQuery(id+"F8.boolean.opBoolean","SPLIT",EDGE,{"disambiguationData":[TD([makeQuery(id+"F5.opExtrude","SWEPT_FACE",FACE,{"disambiguationData":[OSD([sQuery(id+"F4.wireOp",EDGE,"E35.filletArc")])]})])],"derivedFrom":makeQuery(id+"F5.opExtrude","CAP_EDGE",EDGE,{"disambiguationData":[OSD([subQ0])],"isStart":false})});}
            var Q4;
            {var subQ0=sQuery(id+"F0.wireOp",EDGE,"E25.7");var subQ1=sQuery(id+"F0.wireOp",EDGE,"E25.1");var subQ2=sQuery(id+"F0.wireOp",EDGE,"E25.6");var subQ3=sQuery(id+"F0.wireOp",EDGE,"E25.5");var subQ4=sQuery(id+"F0.wireOp",EDGE,"E25.4");var subQ5=sQuery(id+"F0.wireOp",EDGE,"E25.0");var subQ6=sQuery(id+"F0.wireOp",EDGE,"E25.2");var subQ7=sQuery(id+"F0.wireOp",EDGE,"E25.3");Q4=makeQuery(id+"F8.boolean.opBoolean","INTERSECT",EDGE,{"derivedFrom":[makeQuery(id+"F5.boolean.opBoolean","SPLIT",FACE,{"disambiguationData":[TD([makeQuery(id+"F2.opExtrude","SWEPT_FACE",FACE,{"disambiguationData":[OSD([subQ5])]})])],"derivedFrom":makeQuery(id+"F3.boolean.opBoolean","COPY",FACE,{"derivedFrom":makeQuery(id+"F3.opExtrude","CAP_FACE",FACE,{"disambiguationData":[OSD([subQ5,subQ1,subQ6,subQ7,subQ4,subQ3,subQ2,subQ0])],"isStart":false})})}),makeQuery(id+"F8.opExtrude","SWEPT_FACE",FACE,{"disambiguationData":[OSD([sQuery(id+"F7.wireOp",EDGE,"E67")])]})]});}
            var Q5;
            Q5=makeQuery(id+"F8.boolean.opBoolean","INTERSECT",EDGE,{"disambiguationData":[OD(0.0)],"derivedFrom":[makeQuery(id+"F5.opExtrude","SWEPT_FACE",FACE,{"disambiguationData":[OSD([sQuery(id+"F4.wireOp",EDGE,"E30")])]}),makeQuery(id+"F8.opExtrude","SWEPT_FACE",FACE,{"disambiguationData":[OSD([sQuery(id+"F7.wireOp",EDGE,"E67")])]})]});
            fillet(context, id + "F14", {"entities" : qUnion([Q0, Q1, Q2, Q3, Q4, Q5]), "radius" : 3 * mm, "tangentPropagation" : true, "allowEdgeOverflow" : false});
        }
        {
            var Q0;
            Q0=makeQuery(id+"F1.opExtrude","CAP_EDGE",EDGE,{"disambiguationData":[OSD([sQuery(id+"F0.wireOp",EDGE,"E1.bottom")])],"isStart":false});
            fillet(context, id + "F15", {"entities" : qUnion([Q0]), "radius" : 2 * mm, "tangentPropagation" : true, "allowEdgeOverflow" : false});
        }
        {
            var Q0;
            {var subQ0=sQuery(id+"F0.wireOp",EDGE,"E21.filletArc");var subQ1=sQuery(id+"F0.wireOp",EDGE,"E7");var subQ2=sQuery(id+"F0.wireOp",EDGE,"E6");var subQ3=sQuery(id+"F0.wireOp",EDGE,"E5");var subQ4=sQuery(id+"F0.wireOp",EDGE,"E4");var subQ5=sQuery(id+"F0.wireOp",EDGE,"E22.filletArc");var subQ6=sQuery(id+"F0.wireOp",EDGE,"E1.bottom");var subQ7=sQuery(id+"F0.wireOp",EDGE,"E1.right");var subQ8=sQuery(id+"F0.wireOp",EDGE,"E1.top");var subQ9=sQuery(id+"F0.wireOp",EDGE,"E1.left");var subQ10=sQuery(id+"F0.wireOp",EDGE,"E23.filletArc");var subQ11=sQuery(id+"F0.wireOp",EDGE,"E24.filletArc");Q0=makeQuery(id+"F2.boolean.opBoolean","SPLIT",FACE,{"disambiguationData":[TD([makeQuery(id+"F1.opExtrude","SWEPT_FACE",FACE,{"disambiguationData":[OSD([subQ6])]})])],"derivedFrom":makeQuery(id+"F1.opExtrude","CAP_FACE",FACE,{"disambiguationData":[OSD([subQ6,subQ8,subQ9,subQ7,subQ4,subQ3,subQ2,subQ1,subQ0,subQ5,subQ10,subQ11])],"isStart":true})});}
            var sketch = newSketch(context, id + "F16", { "sketchPlane" : qUnion([Q0])});
            skLineSegment(sketch, "E79", {"start": v(0, 90) * mm, "end": v(0, 120) * mm, "construction": true});
            skCircle(sketch, "E80", {"center": v(0, 120) * mm, "radius": 6 * mm});
            skArc(sketch, "E81", {"start": v(15, 120) * mm, "mid": v(0, 135) * mm, "end": v(-15, 120) * mm});
            skLineSegment(sketch, "E82", {"start": v(-15, 120) * mm, "end": v(-15, 108) * mm});
            skLineSegment(sketch, "E83", {"start": v(-15, 108) * mm, "end": v(-33, 90) * mm});
            skLineSegment(sketch, "E84", {"start": v(15, 120) * mm, "end": v(15, 108) * mm});
            skLineSegment(sketch, "E85", {"start": v(15, 108) * mm, "end": v(33, 90) * mm});
            skLineSegment(sketch, "E86", {"start": v(-104.68, 0) * mm, "end": v(127.12, 0) * mm, "construction": true});
            skArc(sketch, "E87.MirrorCS", {"start": v(-15, 120) * mm, "mid": v(0, 135) * mm, "end": v(15, 120) * mm});
            skCircle(sketch, "E88.MirrorC", {"center": v(0, 104.25) * mm, "radius": 6 * mm});
            skLineSegment(sketch, "E89.MirrorCS", {"start": v(15, 108) * mm, "end": v(40.88, 82.12) * mm});
            skLineSegment(sketch, "E90.MirrorCS", {"start": v(-15, -108) * mm, "end": v(-33, -90) * mm});
            skLineSegment(sketch, "E91.MirrorCS", {"start": v(-15, -120) * mm, "end": v(-15, -108) * mm});
            skArc(sketch, "E92.MirrorCS", {"start": v(-15, -120) * mm, "mid": v(0, -135) * mm, "end": v(15, -120) * mm});
            skLineSegment(sketch, "E93.MirrorCS", {"start": v(15, -108) * mm, "end": v(33, -90) * mm});
            skCircle(sketch, "E94.MirrorC", {"center": v(0, -104.25) * mm, "radius": 6 * mm});
            skLineSegment(sketch, "E95.MirrorCS", {"start": v(15, -120) * mm, "end": v(15, -108) * mm});
            skCircle(sketch, "E96.MirrorC", {"center": v(0, -120) * mm, "radius": 6 * mm});
            skLineSegment(sketch, "E97.MirrorCS", {"start": v(15, -108) * mm, "end": v(40.88, -82.12) * mm});
            skArc(sketch, "E98.MirrorCS", {"start": v(15, -120) * mm, "mid": v(0, -135) * mm, "end": v(-15, -120) * mm});
            skLineSegment(sketch, "E99.MirrorCS", {"start": v(0, -90) * mm, "end": v(0, -120) * mm, "construction": true});
            skSolve(sketch);
        }
        {
            var Q0;
            Q0 = qSketchRegion(id + "F16", true);
            var Q1;
            Q1=makeQuery(id+"F2.opExtrude","CAP_FACE",FACE,{"disambiguationData":[OSD([sQuery(id+"F0.wireOp",EDGE,"E12"),sQuery(id+"F0.wireOp",EDGE,"E13"),sQuery(id+"F0.wireOp",EDGE,"E14"),sQuery(id+"F0.wireOp",EDGE,"E15"),sQuery(id+"F0.wireOp",EDGE,"E17.filletArc"),sQuery(id+"F0.wireOp",EDGE,"E18.filletArc"),sQuery(id+"F0.wireOp",EDGE,"E19.filletArc"),sQuery(id+"F0.wireOp",EDGE,"E20.filletArc"),sQuery(id+"F0.wireOp",EDGE,"E25.0"),sQuery(id+"F0.wireOp",EDGE,"E25.1"),sQuery(id+"F0.wireOp",EDGE,"E25.2"),sQuery(id+"F0.wireOp",EDGE,"E25.3"),sQuery(id+"F0.wireOp",EDGE,"E25.4"),sQuery(id+"F0.wireOp",EDGE,"E25.5"),sQuery(id+"F0.wireOp",EDGE,"E25.6"),sQuery(id+"F0.wireOp",EDGE,"E25.7")])],"isStart":false});
            extrude(context, id + "F17", {"entities" : qUnion([Q0]), "endBound" : BoundingType.UP_TO_SURFACE, "endBoundEntityFace" : qUnion([Q1]), "depth" : 25 * mm});
        }
    });
